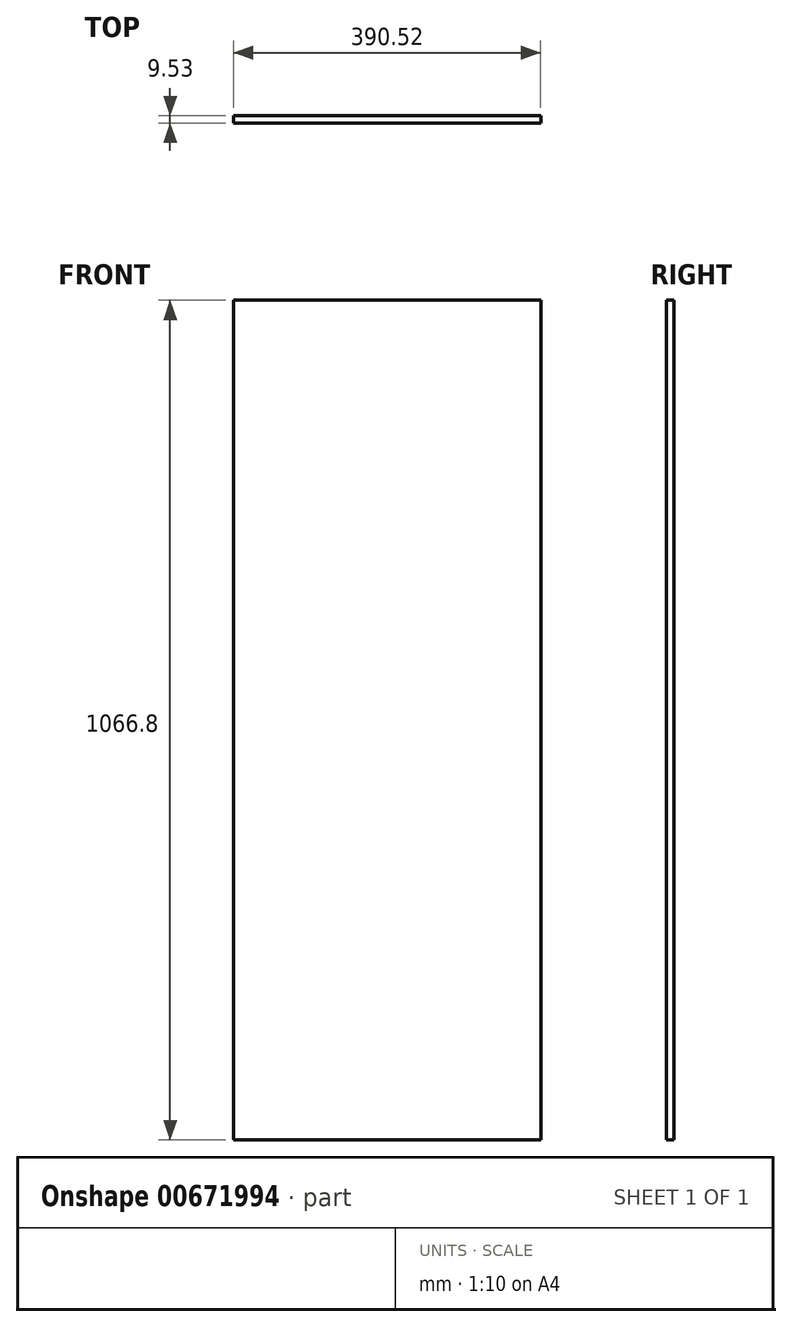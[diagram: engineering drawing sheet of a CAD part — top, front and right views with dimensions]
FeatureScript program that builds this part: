
annotation { "Feature Type Name" : "Feature", "Feature Type Description" : "" }
export const myFeature = defineFeature(function(context is Context, id is Id, definition is map)
    precondition{}
    {
        {
            var Q0;
            Q0=qCreatedBy(makeId("Front.planeOp"),FACE);
            var sketch = newSketch(context, id + "F0", { "sketchPlane" : qUnion([Q0])});
            skLineSegment(sketch, "E0.bottom", {"start": v(195.26, -533.4) * mm, "end": v(-195.26, -533.4) * mm});
            skLineSegment(sketch, "E0.top", {"start": v(195.26, 533.4) * mm, "end": v(-195.26, 533.4) * mm});
            skLineSegment(sketch, "E0.left", {"start": v(195.26, -533.4) * mm, "end": v(195.26, 533.4) * mm});
            skLineSegment(sketch, "E0.right", {"start": v(-195.26, -533.4) * mm, "end": v(-195.26, 533.4) * mm});
            skPoint(sketch, "E0.middle", {"position": v(0, 0) * mm});
            skSolve(sketch);
        }
        {
            var Q0;
            Q0 = qSketchRegion(id + "F0", true);
            extrude(context, id + "F1", {"entities" : qUnion([Q0]), "depth" : 9.52 * mm, "offsetDistance" : 25.4 * mm});
        }
    });
